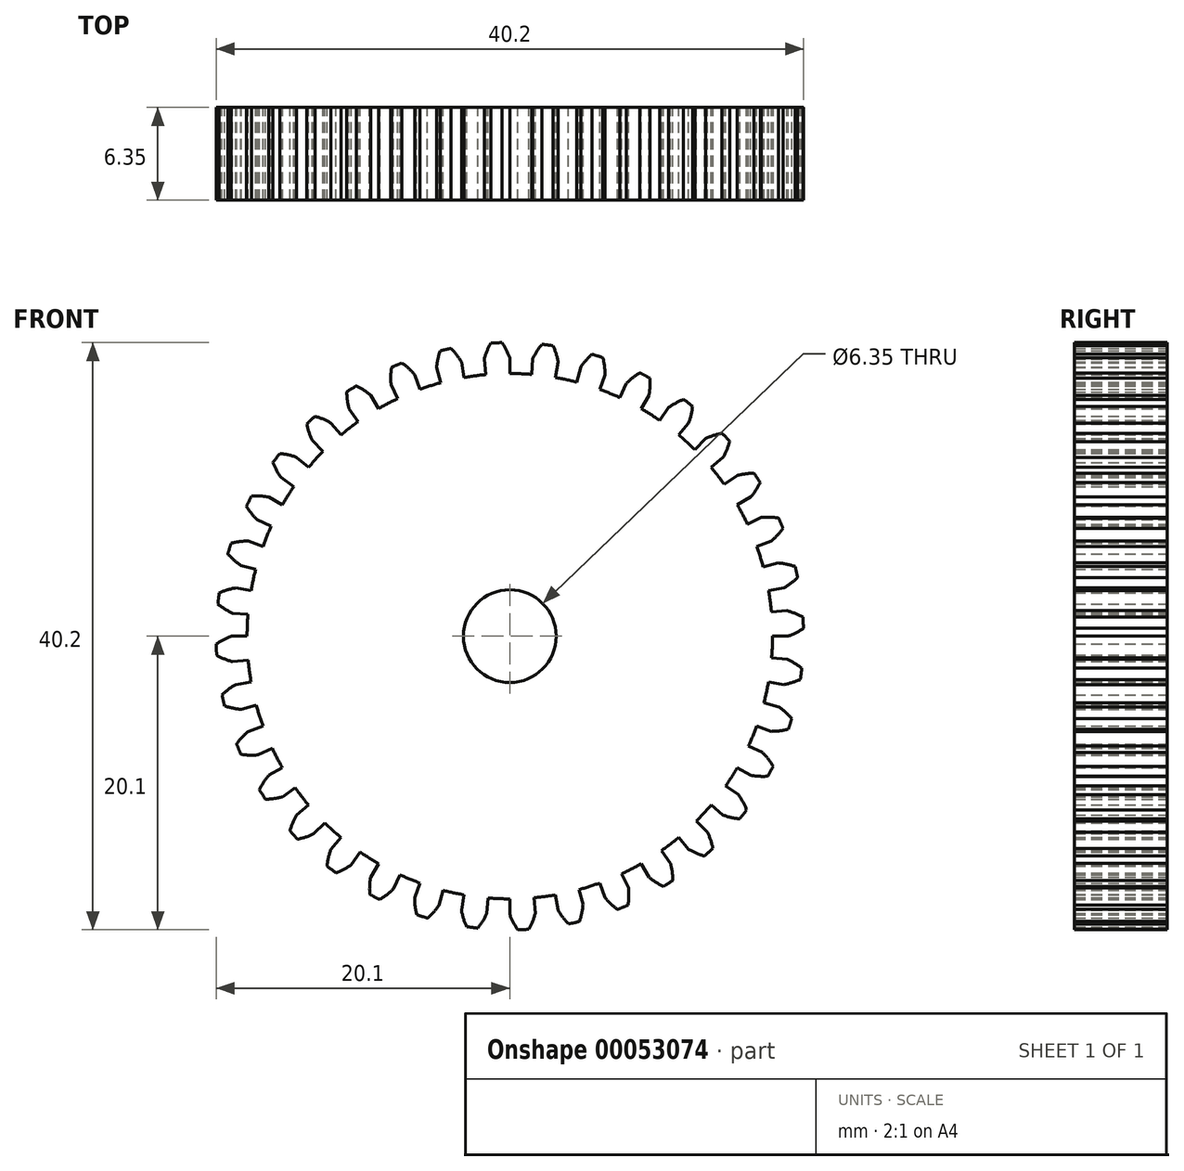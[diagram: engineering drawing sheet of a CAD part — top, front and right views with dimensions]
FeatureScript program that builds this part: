
annotation { "Feature Type Name" : "Feature", "Feature Type Description" : "" }
export const myFeature = defineFeature(function(context is Context, id is Id, definition is map)
    precondition{}
    {
        {
            var Q0;
            Q0=qCreatedBy(makeId("Front.planeOp"),FACE);
            var sketch = newSketch(context, id + "F0", { "sketchPlane" : qUnion([Q0])});
            skArc(sketch, "E0", {"start": v(17.92, -1.49) * mm, "mid": v(17.97, -0.74) * mm, "end": v(17.98, 0) * mm});
            skArc(sketch, "E1", {"start": v(-0.54, 20.1) * mm, "mid": v(-0.92, 20.08) * mm, "end": v(-1.3, 20.06) * mm});
            skLineSegment(sketch, "E2", {"start": v(0, 0) * mm, "end": v(0, 19.05) * mm, "construction": true});
            skArc(sketch, "E3", {"start": v(-8.89, 15.63) * mm, "mid": v(-8.87, 15.6) * mm, "end": v(-8.86, 15.56) * mm});
            skLineSegment(sketch, "E4", {"start": v(0, 19.05) * mm, "end": v(0, 17.98) * mm});
            skArc(sketch, "E5.trimOffspring", {"start": v(0, 19.05) * mm, "mid": v(-0.24, 19.6) * mm, "end": v(-0.54, 20.1) * mm});
            skArc(sketch, "E6.trimOffspring", {"start": v(4.45, 17.34) * mm, "mid": v(4.46, 17.38) * mm, "end": v(4.47, 17.42) * mm});
            skArc(sketch, "E7.MirrorCS", {"start": v(-1.74, 18.97) * mm, "mid": v(-1.56, 19.53) * mm, "end": v(-1.3, 20.06) * mm});
            skLineSegment(sketch, "E8.MirrorCS", {"start": v(-1.74, 18.97) * mm, "end": v(-1.65, 17.9) * mm});
            skLineSegment(sketch, "E9.1.0", {"start": v(-5.01, 18.38) * mm, "end": v(-4.73, 17.35) * mm});
            skArc(sketch, "E9.1.1", {"start": v(-5.01, 18.38) * mm, "mid": v(-4.93, 18.96) * mm, "end": v(-4.77, 19.53) * mm});
            skArc(sketch, "E9.1.2", {"start": v(-4.02, 19.7) * mm, "mid": v(-4.4, 19.62) * mm, "end": v(-4.77, 19.53) * mm});
            skArc(sketch, "E9.1.3", {"start": v(-3.3, 18.76) * mm, "mid": v(-3.63, 19.25) * mm, "end": v(-4.02, 19.7) * mm});
            skLineSegment(sketch, "E9.1.4", {"start": v(-3.3, 18.76) * mm, "end": v(-3.12, 17.7) * mm});
            skLineSegment(sketch, "E9.2.0", {"start": v(-8.13, 17.23) * mm, "end": v(-7.67, 16.26) * mm});
            skArc(sketch, "E9.2.1", {"start": v(-8.13, 17.23) * mm, "mid": v(-8.15, 17.82) * mm, "end": v(-8.09, 18.4) * mm});
            skArc(sketch, "E9.2.2", {"start": v(-7.38, 18.7) * mm, "mid": v(-7.73, 18.56) * mm, "end": v(-8.09, 18.4) * mm});
            skArc(sketch, "E9.2.3", {"start": v(-6.52, 17.9) * mm, "mid": v(-6.92, 18.33) * mm, "end": v(-7.38, 18.7) * mm});
            skLineSegment(sketch, "E9.2.4", {"start": v(-6.52, 17.9) * mm, "end": v(-6.15, 16.9) * mm});
            skLineSegment(sketch, "E10.2.3.0", {"start": v(-11, 15.56) * mm, "end": v(-10.38, 14.69) * mm});
            skArc(sketch, "E10.3.3.0", {"start": v(-11, 15.56) * mm, "mid": v(-11.12, 16.13) * mm, "end": v(-11.16, 16.72) * mm});
            skArc(sketch, "E10.7.3.0", {"start": v(-10.51, 17.14) * mm, "mid": v(-10.84, 16.93) * mm, "end": v(-11.16, 16.72) * mm});
            skArc(sketch, "E10.11.3.0", {"start": v(-9.52, 16.5) * mm, "mid": v(-10, 16.85) * mm, "end": v(-10.51, 17.14) * mm});
            skLineSegment(sketch, "E10.15.3.0", {"start": v(-9.52, 16.5) * mm, "end": v(-9, 15.57) * mm});
            skLineSegment(sketch, "E10.2.4.0", {"start": v(-13.53, 13.41) * mm, "end": v(-12.77, 12.66) * mm});
            skArc(sketch, "E10.3.4.0", {"start": v(-13.53, 13.41) * mm, "mid": v(-13.75, 13.96) * mm, "end": v(-13.9, 14.53) * mm});
            skArc(sketch, "E10.7.4.0", {"start": v(-13.33, 15.05) * mm, "mid": v(-13.62, 14.8) * mm, "end": v(-13.9, 14.53) * mm});
            skArc(sketch, "E10.11.4.0", {"start": v(-12.25, 14.6) * mm, "mid": v(-12.77, 14.86) * mm, "end": v(-13.33, 15.05) * mm});
            skLineSegment(sketch, "E10.15.4.0", {"start": v(-12.25, 14.6) * mm, "end": v(-11.56, 13.78) * mm});
            skLineSegment(sketch, "E10.2.5.0", {"start": v(-15.65, 10.86) * mm, "end": v(-14.78, 10.25) * mm});
            skArc(sketch, "E10.3.5.0", {"start": v(-15.65, 10.86) * mm, "mid": v(-15.96, 11.36) * mm, "end": v(-16.2, 11.9) * mm});
            skArc(sketch, "E10.7.5.0", {"start": v(-15.74, 12.5) * mm, "mid": v(-15.98, 12.2) * mm, "end": v(-16.2, 11.9) * mm});
            skArc(sketch, "E10.11.5.0", {"start": v(-14.6, 12.25) * mm, "mid": v(-15.16, 12.41) * mm, "end": v(-15.74, 12.5) * mm});
            skLineSegment(sketch, "E10.15.5.0", {"start": v(-14.6, 12.25) * mm, "end": v(-13.78, 11.56) * mm});
            skLineSegment(sketch, "E10.2.6.0", {"start": v(-17.3, 7.97) * mm, "end": v(-16.33, 7.53) * mm});
            skArc(sketch, "E10.3.6.0", {"start": v(-17.3, 7.97) * mm, "mid": v(-17.7, 8.41) * mm, "end": v(-18.03, 8.9) * mm});
            skArc(sketch, "E10.7.6.0", {"start": v(-17.67, 9.58) * mm, "mid": v(-17.85, 9.24) * mm, "end": v(-18.03, 8.9) * mm});
            skArc(sketch, "E10.11.6.0", {"start": v(-16.5, 9.53) * mm, "mid": v(-17.08, 9.6) * mm, "end": v(-17.67, 9.58) * mm});
            skLineSegment(sketch, "E10.15.6.0", {"start": v(-16.5, 9.53) * mm, "end": v(-15.57, 9) * mm});
            skLineSegment(sketch, "E10.2.7.0", {"start": v(-18.42, 4.85) * mm, "end": v(-17.4, 4.58) * mm});
            skArc(sketch, "E10.3.7.0", {"start": v(-18.42, 4.85) * mm, "mid": v(-18.88, 5.21) * mm, "end": v(-19.3, 5.63) * mm});
            skArc(sketch, "E10.7.7.0", {"start": v(-19.07, 6.37) * mm, "mid": v(-19.19, 6) * mm, "end": v(-19.3, 5.63) * mm});
            skArc(sketch, "E10.11.7.0", {"start": v(-17.9, 6.52) * mm, "mid": v(-18.49, 6.48) * mm, "end": v(-19.07, 6.37) * mm});
            skLineSegment(sketch, "E10.15.7.0", {"start": v(-17.9, 6.52) * mm, "end": v(-16.9, 6.15) * mm});
            skLineSegment(sketch, "E10.2.8.0", {"start": v(-18.98, 1.58) * mm, "end": v(-17.92, 1.49) * mm});
            skArc(sketch, "E10.3.8.0", {"start": v(-18.98, 1.58) * mm, "mid": v(-19.5, 1.86) * mm, "end": v(-19.98, 2.2) * mm});
            skArc(sketch, "E10.7.8.0", {"start": v(-19.88, 2.96) * mm, "mid": v(-19.94, 2.58) * mm, "end": v(-19.98, 2.2) * mm});
            skArc(sketch, "E10.11.8.0", {"start": v(-18.76, 3.3) * mm, "mid": v(-19.33, 3.17) * mm, "end": v(-19.88, 2.96) * mm});
            skLineSegment(sketch, "E10.15.8.0", {"start": v(-18.76, 3.3) * mm, "end": v(-17.7, 3.12) * mm});
            skLineSegment(sketch, "E10.2.9.0", {"start": v(-18.97, -1.74) * mm, "end": v(-17.9, -1.65) * mm});
            skArc(sketch, "E10.3.9.0", {"start": v(-18.97, -1.74) * mm, "mid": v(-19.53, -1.56) * mm, "end": v(-20.06, -1.3) * mm});
            skArc(sketch, "E10.7.9.0", {"start": v(-20.1, -0.54) * mm, "mid": v(-20.08, -0.92) * mm, "end": v(-20.06, -1.3) * mm});
            skArc(sketch, "E10.11.9.0", {"start": v(-19.05, 0) * mm, "mid": v(-19.6, -0.24) * mm, "end": v(-20.1, -0.54) * mm});
            skLineSegment(sketch, "E10.15.9.0", {"start": v(-19.05, 0) * mm, "end": v(-17.98, 0) * mm});
            skLineSegment(sketch, "E10.2.10.0", {"start": v(-18.38, -5.01) * mm, "end": v(-17.35, -4.73) * mm});
            skArc(sketch, "E10.3.10.0", {"start": v(-18.38, -5.01) * mm, "mid": v(-18.96, -4.93) * mm, "end": v(-19.53, -4.77) * mm});
            skArc(sketch, "E10.7.10.0", {"start": v(-19.7, -4.02) * mm, "mid": v(-19.62, -4.4) * mm, "end": v(-19.53, -4.77) * mm});
            skArc(sketch, "E10.11.10.0", {"start": v(-18.76, -3.3) * mm, "mid": v(-19.25, -3.63) * mm, "end": v(-19.7, -4.02) * mm});
            skLineSegment(sketch, "E10.15.10.0", {"start": v(-18.76, -3.3) * mm, "end": v(-17.7, -3.12) * mm});
            skLineSegment(sketch, "E10.2.11.0", {"start": v(-17.23, -8.13) * mm, "end": v(-16.26, -7.67) * mm});
            skArc(sketch, "E10.3.11.0", {"start": v(-17.23, -8.13) * mm, "mid": v(-17.82, -8.15) * mm, "end": v(-18.4, -8.09) * mm});
            skArc(sketch, "E10.7.11.0", {"start": v(-18.7, -7.38) * mm, "mid": v(-18.56, -7.73) * mm, "end": v(-18.4, -8.09) * mm});
            skArc(sketch, "E10.11.11.0", {"start": v(-17.9, -6.52) * mm, "mid": v(-18.33, -6.92) * mm, "end": v(-18.7, -7.38) * mm});
            skLineSegment(sketch, "E10.15.11.0", {"start": v(-17.9, -6.52) * mm, "end": v(-16.9, -6.15) * mm});
            skLineSegment(sketch, "E10.2.12.0", {"start": v(-15.56, -11) * mm, "end": v(-14.69, -10.38) * mm});
            skArc(sketch, "E10.3.12.0", {"start": v(-15.56, -11) * mm, "mid": v(-16.13, -11.12) * mm, "end": v(-16.72, -11.16) * mm});
            skArc(sketch, "E10.7.12.0", {"start": v(-17.14, -10.51) * mm, "mid": v(-16.93, -10.84) * mm, "end": v(-16.72, -11.16) * mm});
            skArc(sketch, "E10.11.12.0", {"start": v(-16.5, -9.52) * mm, "mid": v(-16.85, -10) * mm, "end": v(-17.14, -10.51) * mm});
            skLineSegment(sketch, "E10.15.12.0", {"start": v(-16.5, -9.52) * mm, "end": v(-15.57, -9) * mm});
            skLineSegment(sketch, "E10.2.13.0", {"start": v(-13.41, -13.53) * mm, "end": v(-12.66, -12.77) * mm});
            skArc(sketch, "E10.3.13.0", {"start": v(-13.41, -13.53) * mm, "mid": v(-13.96, -13.75) * mm, "end": v(-14.53, -13.9) * mm});
            skArc(sketch, "E10.7.13.0", {"start": v(-15.05, -13.33) * mm, "mid": v(-14.8, -13.62) * mm, "end": v(-14.53, -13.9) * mm});
            skArc(sketch, "E10.11.13.0", {"start": v(-14.6, -12.25) * mm, "mid": v(-14.86, -12.77) * mm, "end": v(-15.05, -13.33) * mm});
            skLineSegment(sketch, "E10.15.13.0", {"start": v(-14.6, -12.25) * mm, "end": v(-13.78, -11.56) * mm});
            skLineSegment(sketch, "E10.2.14.0", {"start": v(-10.86, -15.65) * mm, "end": v(-10.25, -14.78) * mm});
            skArc(sketch, "E10.3.14.0", {"start": v(-10.86, -15.65) * mm, "mid": v(-11.36, -15.96) * mm, "end": v(-11.9, -16.2) * mm});
            skArc(sketch, "E10.7.14.0", {"start": v(-12.5, -15.74) * mm, "mid": v(-12.2, -15.98) * mm, "end": v(-11.9, -16.2) * mm});
            skArc(sketch, "E10.11.14.0", {"start": v(-12.25, -14.6) * mm, "mid": v(-12.41, -15.16) * mm, "end": v(-12.5, -15.74) * mm});
            skLineSegment(sketch, "E10.15.14.0", {"start": v(-12.25, -14.6) * mm, "end": v(-11.56, -13.78) * mm});
            skLineSegment(sketch, "E10.2.15.0", {"start": v(-7.97, -17.3) * mm, "end": v(-7.53, -16.33) * mm});
            skArc(sketch, "E10.3.15.0", {"start": v(-7.97, -17.3) * mm, "mid": v(-8.41, -17.7) * mm, "end": v(-8.9, -18.03) * mm});
            skArc(sketch, "E10.7.15.0", {"start": v(-9.58, -17.67) * mm, "mid": v(-9.24, -17.85) * mm, "end": v(-8.9, -18.03) * mm});
            skArc(sketch, "E10.11.15.0", {"start": v(-9.53, -16.5) * mm, "mid": v(-9.6, -17.08) * mm, "end": v(-9.58, -17.67) * mm});
            skLineSegment(sketch, "E10.15.15.0", {"start": v(-9.53, -16.5) * mm, "end": v(-9, -15.57) * mm});
            skLineSegment(sketch, "E10.2.16.0", {"start": v(-4.85, -18.42) * mm, "end": v(-4.58, -17.4) * mm});
            skArc(sketch, "E10.3.16.0", {"start": v(-4.85, -18.42) * mm, "mid": v(-5.21, -18.88) * mm, "end": v(-5.63, -19.3) * mm});
            skArc(sketch, "E10.7.16.0", {"start": v(-6.37, -19.07) * mm, "mid": v(-6, -19.19) * mm, "end": v(-5.63, -19.3) * mm});
            skArc(sketch, "E10.11.16.0", {"start": v(-6.52, -17.9) * mm, "mid": v(-6.48, -18.49) * mm, "end": v(-6.37, -19.07) * mm});
            skLineSegment(sketch, "E10.15.16.0", {"start": v(-6.52, -17.9) * mm, "end": v(-6.15, -16.9) * mm});
            skLineSegment(sketch, "E10.2.17.0", {"start": v(-1.58, -18.98) * mm, "end": v(-1.49, -17.92) * mm});
            skArc(sketch, "E10.3.17.0", {"start": v(-1.58, -18.98) * mm, "mid": v(-1.86, -19.5) * mm, "end": v(-2.2, -19.98) * mm});
            skArc(sketch, "E10.7.17.0", {"start": v(-2.96, -19.88) * mm, "mid": v(-2.58, -19.94) * mm, "end": v(-2.2, -19.98) * mm});
            skArc(sketch, "E10.11.17.0", {"start": v(-3.3, -18.76) * mm, "mid": v(-3.17, -19.33) * mm, "end": v(-2.96, -19.88) * mm});
            skLineSegment(sketch, "E10.15.17.0", {"start": v(-3.3, -18.76) * mm, "end": v(-3.12, -17.7) * mm});
            skLineSegment(sketch, "E10.2.18.0", {"start": v(1.74, -18.97) * mm, "end": v(1.65, -17.9) * mm});
            skArc(sketch, "E10.3.18.0", {"start": v(1.74, -18.97) * mm, "mid": v(1.56, -19.53) * mm, "end": v(1.3, -20.06) * mm});
            skArc(sketch, "E10.7.18.0", {"start": v(0.54, -20.1) * mm, "mid": v(0.92, -20.08) * mm, "end": v(1.3, -20.06) * mm});
            skArc(sketch, "E10.11.18.0", {"start": v(0, -19.05) * mm, "mid": v(0.24, -19.6) * mm, "end": v(0.54, -20.1) * mm});
            skLineSegment(sketch, "E10.15.18.0", {"start": v(0, -19.05) * mm, "end": v(0, -17.98) * mm});
            skLineSegment(sketch, "E10.2.19.0", {"start": v(5.01, -18.38) * mm, "end": v(4.73, -17.35) * mm});
            skArc(sketch, "E10.3.19.0", {"start": v(5.01, -18.38) * mm, "mid": v(4.93, -18.96) * mm, "end": v(4.77, -19.53) * mm});
            skArc(sketch, "E10.7.19.0", {"start": v(4.02, -19.7) * mm, "mid": v(4.4, -19.62) * mm, "end": v(4.77, -19.53) * mm});
            skArc(sketch, "E10.11.19.0", {"start": v(3.3, -18.76) * mm, "mid": v(3.63, -19.25) * mm, "end": v(4.02, -19.7) * mm});
            skLineSegment(sketch, "E10.15.19.0", {"start": v(3.3, -18.76) * mm, "end": v(3.12, -17.7) * mm});
            skLineSegment(sketch, "E10.2.20.0", {"start": v(8.13, -17.23) * mm, "end": v(7.67, -16.26) * mm});
            skArc(sketch, "E10.3.20.0", {"start": v(8.13, -17.23) * mm, "mid": v(8.15, -17.82) * mm, "end": v(8.09, -18.4) * mm});
            skArc(sketch, "E10.7.20.0", {"start": v(7.38, -18.7) * mm, "mid": v(7.73, -18.56) * mm, "end": v(8.09, -18.4) * mm});
            skArc(sketch, "E10.11.20.0", {"start": v(6.52, -17.9) * mm, "mid": v(6.92, -18.33) * mm, "end": v(7.38, -18.7) * mm});
            skLineSegment(sketch, "E10.15.20.0", {"start": v(6.52, -17.9) * mm, "end": v(6.15, -16.9) * mm});
            skLineSegment(sketch, "E10.2.21.0", {"start": v(11, -15.56) * mm, "end": v(10.38, -14.69) * mm});
            skArc(sketch, "E10.3.21.0", {"start": v(11, -15.56) * mm, "mid": v(11.12, -16.13) * mm, "end": v(11.16, -16.72) * mm});
            skArc(sketch, "E10.7.21.0", {"start": v(10.51, -17.14) * mm, "mid": v(10.84, -16.93) * mm, "end": v(11.16, -16.72) * mm});
            skArc(sketch, "E10.11.21.0", {"start": v(9.52, -16.5) * mm, "mid": v(10, -16.85) * mm, "end": v(10.51, -17.14) * mm});
            skLineSegment(sketch, "E10.15.21.0", {"start": v(9.53, -16.5) * mm, "end": v(9, -15.57) * mm});
            skLineSegment(sketch, "E10.2.22.0", {"start": v(13.53, -13.41) * mm, "end": v(12.77, -12.66) * mm});
            skArc(sketch, "E10.3.22.0", {"start": v(13.53, -13.41) * mm, "mid": v(13.75, -13.96) * mm, "end": v(13.9, -14.53) * mm});
            skArc(sketch, "E10.7.22.0", {"start": v(13.33, -15.05) * mm, "mid": v(13.62, -14.8) * mm, "end": v(13.9, -14.53) * mm});
            skArc(sketch, "E10.11.22.0", {"start": v(12.25, -14.6) * mm, "mid": v(12.77, -14.86) * mm, "end": v(13.33, -15.05) * mm});
            skLineSegment(sketch, "E10.15.22.0", {"start": v(12.25, -14.6) * mm, "end": v(11.56, -13.78) * mm});
            skLineSegment(sketch, "E10.2.23.0", {"start": v(15.65, -10.86) * mm, "end": v(14.78, -10.25) * mm});
            skArc(sketch, "E10.3.23.0", {"start": v(15.65, -10.86) * mm, "mid": v(15.96, -11.36) * mm, "end": v(16.2, -11.9) * mm});
            skArc(sketch, "E10.7.23.0", {"start": v(15.74, -12.5) * mm, "mid": v(15.98, -12.2) * mm, "end": v(16.2, -11.9) * mm});
            skArc(sketch, "E10.11.23.0", {"start": v(14.6, -12.25) * mm, "mid": v(15.16, -12.41) * mm, "end": v(15.74, -12.5) * mm});
            skLineSegment(sketch, "E10.15.23.0", {"start": v(14.6, -12.25) * mm, "end": v(13.78, -11.56) * mm});
            skLineSegment(sketch, "E10.2.24.0", {"start": v(17.3, -7.97) * mm, "end": v(16.33, -7.53) * mm});
            skArc(sketch, "E10.3.24.0", {"start": v(17.3, -7.97) * mm, "mid": v(17.7, -8.41) * mm, "end": v(18.03, -8.9) * mm});
            skArc(sketch, "E10.7.24.0", {"start": v(17.67, -9.58) * mm, "mid": v(17.85, -9.24) * mm, "end": v(18.03, -8.9) * mm});
            skArc(sketch, "E10.11.24.0", {"start": v(16.5, -9.53) * mm, "mid": v(17.08, -9.6) * mm, "end": v(17.67, -9.58) * mm});
            skLineSegment(sketch, "E10.15.24.0", {"start": v(16.5, -9.53) * mm, "end": v(15.57, -9) * mm});
            skLineSegment(sketch, "E10.2.25.0", {"start": v(18.42, -4.85) * mm, "end": v(17.4, -4.58) * mm});
            skArc(sketch, "E10.3.25.0", {"start": v(18.42, -4.85) * mm, "mid": v(18.88, -5.21) * mm, "end": v(19.3, -5.63) * mm});
            skArc(sketch, "E10.7.25.0", {"start": v(19.07, -6.37) * mm, "mid": v(19.19, -6) * mm, "end": v(19.3, -5.63) * mm});
            skArc(sketch, "E10.11.25.0", {"start": v(17.9, -6.52) * mm, "mid": v(18.49, -6.48) * mm, "end": v(19.07, -6.37) * mm});
            skLineSegment(sketch, "E10.15.25.0", {"start": v(17.9, -6.52) * mm, "end": v(16.9, -6.15) * mm});
            skLineSegment(sketch, "E10.2.26.0", {"start": v(18.98, -1.58) * mm, "end": v(17.92, -1.49) * mm});
            skArc(sketch, "E10.3.26.0", {"start": v(18.98, -1.58) * mm, "mid": v(19.5, -1.86) * mm, "end": v(19.98, -2.2) * mm});
            skArc(sketch, "E10.7.26.0", {"start": v(19.88, -2.96) * mm, "mid": v(19.94, -2.58) * mm, "end": v(19.98, -2.2) * mm});
            skArc(sketch, "E10.11.26.0", {"start": v(18.76, -3.3) * mm, "mid": v(19.33, -3.17) * mm, "end": v(19.88, -2.96) * mm});
            skLineSegment(sketch, "E10.15.26.0", {"start": v(18.76, -3.3) * mm, "end": v(17.7, -3.12) * mm});
            skLineSegment(sketch, "E10.2.27.0", {"start": v(18.97, 1.74) * mm, "end": v(17.9, 1.65) * mm});
            skArc(sketch, "E10.3.27.0", {"start": v(18.97, 1.74) * mm, "mid": v(19.53, 1.56) * mm, "end": v(20.06, 1.3) * mm});
            skArc(sketch, "E10.7.27.0", {"start": v(20.1, 0.54) * mm, "mid": v(20.08, 0.92) * mm, "end": v(20.06, 1.3) * mm});
            skArc(sketch, "E10.11.27.0", {"start": v(19.05, 0) * mm, "mid": v(19.6, 0.24) * mm, "end": v(20.1, 0.54) * mm});
            skLineSegment(sketch, "E10.15.27.0", {"start": v(19.05, 0) * mm, "end": v(17.98, 0) * mm});
            skLineSegment(sketch, "E10.2.28.0", {"start": v(18.38, 5.01) * mm, "end": v(17.35, 4.73) * mm});
            skArc(sketch, "E10.3.28.0", {"start": v(18.38, 5.01) * mm, "mid": v(18.96, 4.93) * mm, "end": v(19.53, 4.77) * mm});
            skArc(sketch, "E10.7.28.0", {"start": v(19.7, 4.02) * mm, "mid": v(19.62, 4.4) * mm, "end": v(19.53, 4.77) * mm});
            skArc(sketch, "E10.11.28.0", {"start": v(18.76, 3.3) * mm, "mid": v(19.25, 3.63) * mm, "end": v(19.7, 4.02) * mm});
            skLineSegment(sketch, "E10.15.28.0", {"start": v(18.76, 3.3) * mm, "end": v(17.7, 3.12) * mm});
            skLineSegment(sketch, "E10.2.29.0", {"start": v(17.23, 8.13) * mm, "end": v(16.26, 7.67) * mm});
            skArc(sketch, "E10.3.29.0", {"start": v(17.23, 8.13) * mm, "mid": v(17.82, 8.15) * mm, "end": v(18.4, 8.09) * mm});
            skArc(sketch, "E10.7.29.0", {"start": v(18.7, 7.38) * mm, "mid": v(18.56, 7.73) * mm, "end": v(18.4, 8.09) * mm});
            skArc(sketch, "E10.11.29.0", {"start": v(17.9, 6.52) * mm, "mid": v(18.33, 6.92) * mm, "end": v(18.7, 7.38) * mm});
            skLineSegment(sketch, "E10.15.29.0", {"start": v(17.9, 6.52) * mm, "end": v(16.9, 6.15) * mm});
            skLineSegment(sketch, "E10.2.30.0", {"start": v(15.56, 11) * mm, "end": v(14.69, 10.38) * mm});
            skArc(sketch, "E10.3.30.0", {"start": v(15.56, 11) * mm, "mid": v(16.13, 11.12) * mm, "end": v(16.72, 11.16) * mm});
            skArc(sketch, "E10.7.30.0", {"start": v(17.14, 10.51) * mm, "mid": v(16.93, 10.84) * mm, "end": v(16.72, 11.16) * mm});
            skArc(sketch, "E10.11.30.0", {"start": v(16.5, 9.52) * mm, "mid": v(16.85, 10) * mm, "end": v(17.14, 10.51) * mm});
            skLineSegment(sketch, "E10.15.30.0", {"start": v(16.5, 9.52) * mm, "end": v(15.57, 9) * mm});
            skLineSegment(sketch, "E10.2.31.0", {"start": v(13.41, 13.53) * mm, "end": v(12.66, 12.77) * mm});
            skArc(sketch, "E10.3.31.0", {"start": v(13.41, 13.53) * mm, "mid": v(13.96, 13.75) * mm, "end": v(14.53, 13.9) * mm});
            skArc(sketch, "E10.7.31.0", {"start": v(15.05, 13.33) * mm, "mid": v(14.8, 13.62) * mm, "end": v(14.53, 13.9) * mm});
            skArc(sketch, "E10.11.31.0", {"start": v(14.6, 12.25) * mm, "mid": v(14.86, 12.77) * mm, "end": v(15.05, 13.33) * mm});
            skLineSegment(sketch, "E10.15.31.0", {"start": v(14.6, 12.25) * mm, "end": v(13.78, 11.56) * mm});
            skLineSegment(sketch, "E10.2.32.0", {"start": v(10.86, 15.65) * mm, "end": v(10.25, 14.78) * mm});
            skArc(sketch, "E10.3.32.0", {"start": v(10.86, 15.65) * mm, "mid": v(11.36, 15.96) * mm, "end": v(11.9, 16.2) * mm});
            skArc(sketch, "E10.7.32.0", {"start": v(12.5, 15.74) * mm, "mid": v(12.2, 15.98) * mm, "end": v(11.9, 16.2) * mm});
            skArc(sketch, "E10.11.32.0", {"start": v(12.25, 14.6) * mm, "mid": v(12.41, 15.16) * mm, "end": v(12.5, 15.74) * mm});
            skLineSegment(sketch, "E10.15.32.0", {"start": v(12.25, 14.6) * mm, "end": v(11.56, 13.78) * mm});
            skLineSegment(sketch, "E10.2.33.0", {"start": v(7.97, 17.3) * mm, "end": v(7.53, 16.33) * mm});
            skArc(sketch, "E10.3.33.0", {"start": v(7.97, 17.3) * mm, "mid": v(8.41, 17.7) * mm, "end": v(8.9, 18.03) * mm});
            skArc(sketch, "E10.7.33.0", {"start": v(9.58, 17.67) * mm, "mid": v(9.24, 17.85) * mm, "end": v(8.9, 18.03) * mm});
            skArc(sketch, "E10.11.33.0", {"start": v(9.52, 16.5) * mm, "mid": v(9.6, 17.08) * mm, "end": v(9.58, 17.67) * mm});
            skLineSegment(sketch, "E10.15.33.0", {"start": v(9.52, 16.5) * mm, "end": v(9, 15.57) * mm});
            skLineSegment(sketch, "E10.2.34.0", {"start": v(4.85, 18.42) * mm, "end": v(4.58, 17.4) * mm});
            skArc(sketch, "E10.3.34.0", {"start": v(4.85, 18.42) * mm, "mid": v(5.21, 18.88) * mm, "end": v(5.63, 19.3) * mm});
            skArc(sketch, "E10.7.34.0", {"start": v(6.37, 19.07) * mm, "mid": v(6, 19.19) * mm, "end": v(5.63, 19.3) * mm});
            skArc(sketch, "E10.11.34.0", {"start": v(6.52, 17.9) * mm, "mid": v(6.48, 18.49) * mm, "end": v(6.37, 19.07) * mm});
            skLineSegment(sketch, "E10.15.34.0", {"start": v(6.52, 17.9) * mm, "end": v(6.15, 16.9) * mm});
            skLineSegment(sketch, "E10.2.35.0", {"start": v(1.58, 18.98) * mm, "end": v(1.49, 17.92) * mm});
            skArc(sketch, "E10.3.35.0", {"start": v(1.58, 18.98) * mm, "mid": v(1.86, 19.5) * mm, "end": v(2.2, 19.98) * mm});
            skArc(sketch, "E10.7.35.0", {"start": v(2.96, 19.88) * mm, "mid": v(2.58, 19.94) * mm, "end": v(2.2, 19.98) * mm});
            skArc(sketch, "E10.11.35.0", {"start": v(3.3, 18.76) * mm, "mid": v(3.17, 19.33) * mm, "end": v(2.96, 19.88) * mm});
            skLineSegment(sketch, "E10.15.35.0", {"start": v(3.3, 18.76) * mm, "end": v(3.12, 17.7) * mm});
            skArc(sketch, "E11.trimOffspring", {"start": v(17.9, 1.65) * mm, "mid": v(17.82, 2.39) * mm, "end": v(17.7, 3.12) * mm});
            skArc(sketch, "E12.trimOffspring", {"start": v(16.33, -7.53) * mm, "mid": v(16.63, -6.84) * mm, "end": v(16.9, -6.15) * mm});
            skArc(sketch, "E13.trimOffspring", {"start": v(17.4, -4.58) * mm, "mid": v(17.57, -3.85) * mm, "end": v(17.7, -3.12) * mm});
            skArc(sketch, "E14.trimOffspring", {"start": v(14.78, -10.25) * mm, "mid": v(15.19, -9.63) * mm, "end": v(15.57, -9) * mm});
            skArc(sketch, "E15.trimOffspring", {"start": v(12.77, -12.66) * mm, "mid": v(13.29, -12.12) * mm, "end": v(13.78, -11.56) * mm});
            skArc(sketch, "E16.trimOffspring", {"start": v(10.38, -14.69) * mm, "mid": v(10.98, -14.24) * mm, "end": v(11.56, -13.78) * mm});
            skArc(sketch, "E17.trimOffspring", {"start": v(7.67, -16.26) * mm, "mid": v(8.34, -15.93) * mm, "end": v(9, -15.57) * mm});
            skArc(sketch, "E18.trimOffspring", {"start": v(4.73, -17.35) * mm, "mid": v(5.45, -17.14) * mm, "end": v(6.15, -16.9) * mm});
            skArc(sketch, "E19.trimOffspring", {"start": v(1.65, -17.9) * mm, "mid": v(2.39, -17.82) * mm, "end": v(3.12, -17.7) * mm});
            skArc(sketch, "E20.trimOffspring", {"start": v(-1.49, -17.92) * mm, "mid": v(-0.74, -17.97) * mm, "end": v(0, -17.98) * mm});
            skArc(sketch, "E21.trimOffspring", {"start": v(-4.58, -17.4) * mm, "mid": v(-3.85, -17.57) * mm, "end": v(-3.12, -17.7) * mm});
            skArc(sketch, "E22.trimOffspring", {"start": v(-7.53, -16.33) * mm, "mid": v(-6.84, -16.63) * mm, "end": v(-6.15, -16.9) * mm});
            skArc(sketch, "E23.trimOffspring", {"start": v(-10.25, -14.78) * mm, "mid": v(-9.63, -15.19) * mm, "end": v(-9, -15.57) * mm});
            skArc(sketch, "E24.trimOffspring", {"start": v(-12.66, -12.77) * mm, "mid": v(-12.12, -13.29) * mm, "end": v(-11.56, -13.78) * mm});
            skArc(sketch, "E25.trimOffspring", {"start": v(-14.69, -10.38) * mm, "mid": v(-14.24, -10.98) * mm, "end": v(-13.78, -11.56) * mm});
            skArc(sketch, "E26.trimOffspring", {"start": v(-16.26, -7.67) * mm, "mid": v(-15.93, -8.34) * mm, "end": v(-15.57, -9) * mm});
            skArc(sketch, "E27.trimOffspring", {"start": v(-17.35, -4.73) * mm, "mid": v(-17.14, -5.45) * mm, "end": v(-16.9, -6.15) * mm});
            skArc(sketch, "E28.trimOffspring", {"start": v(-17.9, -1.65) * mm, "mid": v(-17.82, -2.39) * mm, "end": v(-17.7, -3.12) * mm});
            skArc(sketch, "E29.trimOffspring", {"start": v(-17.92, 1.49) * mm, "mid": v(-17.97, 0.74) * mm, "end": v(-17.98, 0) * mm});
            skArc(sketch, "E30.trimOffspring", {"start": v(-17.4, 4.58) * mm, "mid": v(-17.57, 3.85) * mm, "end": v(-17.7, 3.12) * mm});
            skArc(sketch, "E31.trimOffspring", {"start": v(-16.33, 7.53) * mm, "mid": v(-16.63, 6.84) * mm, "end": v(-16.9, 6.15) * mm});
            skArc(sketch, "E32.trimOffspring", {"start": v(-14.78, 10.25) * mm, "mid": v(-15.19, 9.63) * mm, "end": v(-15.57, 9) * mm});
            skArc(sketch, "E33.trimOffspring", {"start": v(-12.77, 12.66) * mm, "mid": v(-13.29, 12.12) * mm, "end": v(-13.78, 11.56) * mm});
            skArc(sketch, "E34.trimOffspring", {"start": v(-10.38, 14.69) * mm, "mid": v(-10.98, 14.24) * mm, "end": v(-11.56, 13.78) * mm});
            skArc(sketch, "E35.trimOffspring", {"start": v(-7.67, 16.26) * mm, "mid": v(-8.34, 15.93) * mm, "end": v(-9, 15.57) * mm});
            skArc(sketch, "E36.trimOffspring", {"start": v(-4.73, 17.35) * mm, "mid": v(-5.45, 17.14) * mm, "end": v(-6.15, 16.9) * mm});
            skArc(sketch, "E37.trimOffspring", {"start": v(-1.57, 17.91) * mm, "mid": v(-2.35, 17.83) * mm, "end": v(-3.12, 17.7) * mm});
            skArc(sketch, "E38.trimOffspring", {"start": v(1.49, 17.92) * mm, "mid": v(0.74, 17.97) * mm, "end": v(0, 17.98) * mm});
            skArc(sketch, "E39.trimOffspring", {"start": v(4.58, 17.4) * mm, "mid": v(3.85, 17.57) * mm, "end": v(3.12, 17.7) * mm});
            skArc(sketch, "E40.trimOffspring", {"start": v(7.53, 16.33) * mm, "mid": v(6.84, 16.63) * mm, "end": v(6.15, 16.9) * mm});
            skArc(sketch, "E41.trimOffspring", {"start": v(10.25, 14.78) * mm, "mid": v(9.63, 15.19) * mm, "end": v(9, 15.57) * mm});
            skArc(sketch, "E42.trimOffspring", {"start": v(12.66, 12.77) * mm, "mid": v(12.12, 13.29) * mm, "end": v(11.56, 13.78) * mm});
            skArc(sketch, "E43.trimOffspring", {"start": v(14.69, 10.38) * mm, "mid": v(14.24, 10.98) * mm, "end": v(13.78, 11.56) * mm});
            skArc(sketch, "E44.trimOffspring", {"start": v(16.26, 7.67) * mm, "mid": v(15.93, 8.34) * mm, "end": v(15.57, 9) * mm});
            skArc(sketch, "E45.trimOffspring", {"start": v(17.35, 4.73) * mm, "mid": v(17.14, 5.45) * mm, "end": v(16.9, 6.15) * mm});
            skCircle(sketch, "E46", {"center": v(0, 0) * mm, "radius": 3.18 * mm});
            skSolve(sketch);
        }
        {
            var Q0;
            Q0 = qSketchRegion(id + "F0", true);
            extrude(context, id + "F1", {"entities" : qUnion([Q0]), "depth" : 6.35 * mm});
        }
    });
